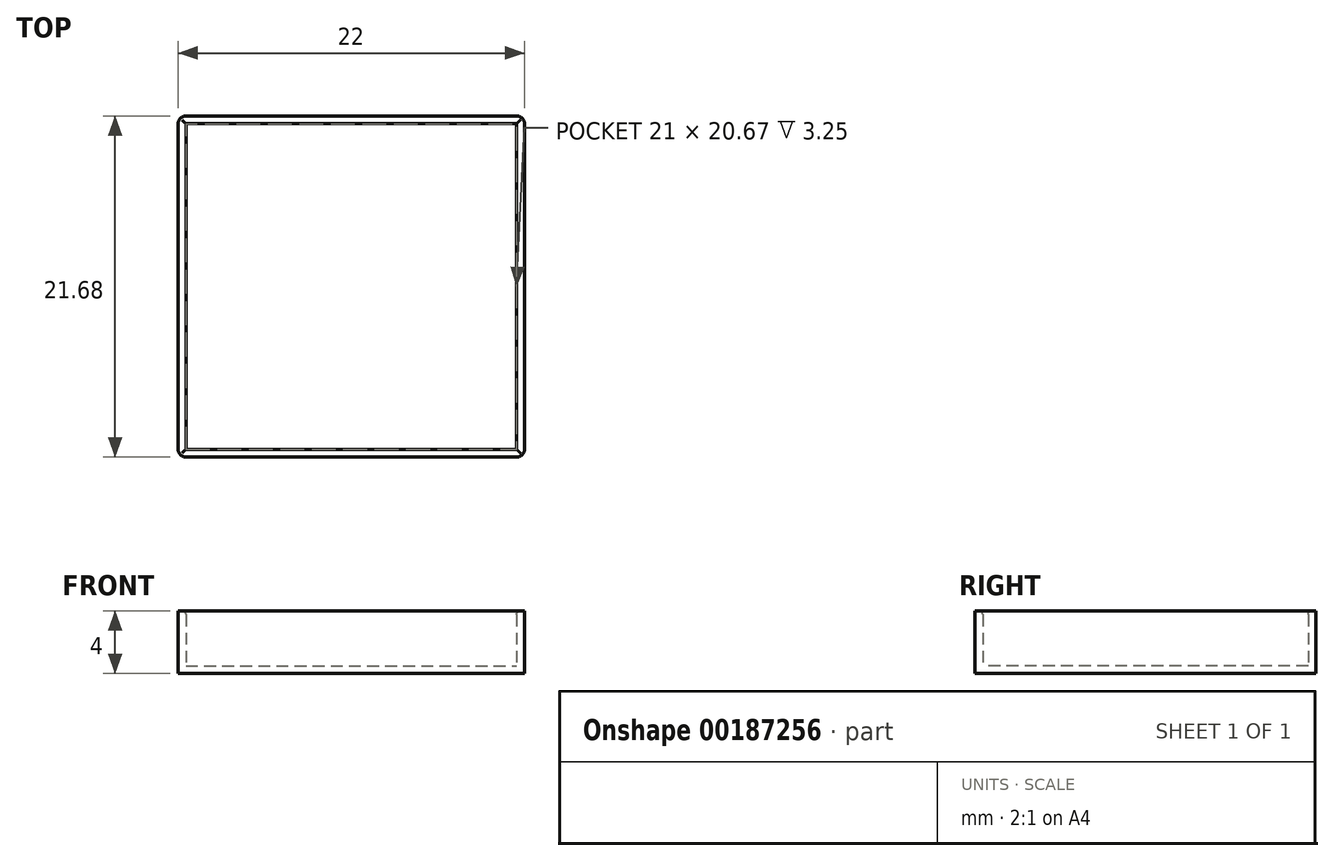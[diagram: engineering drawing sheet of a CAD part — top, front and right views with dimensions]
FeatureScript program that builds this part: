
annotation { "Feature Type Name" : "Feature", "Feature Type Description" : "" }
export const myFeature = defineFeature(function(context is Context, id is Id, definition is map)
    precondition{}
    {
        {
            var Q0;
            Q0=qCreatedBy(makeId("Top.planeOp"),FACE);
            var sketch = newSketch(context, id + "F0", { "sketchPlane" : qUnion([Q0])});
            skLineSegment(sketch, "E0.bottom", {"start": v(-10.5, 10.84) * mm, "end": v(10.5, 10.84) * mm});
            skLineSegment(sketch, "E0.top", {"start": v(-10.5, -10.84) * mm, "end": v(10.5, -10.84) * mm});
            skLineSegment(sketch, "E0.left", {"start": v(-11, 10.34) * mm, "end": v(-11, -10.34) * mm});
            skLineSegment(sketch, "E0.right", {"start": v(11, 10.34) * mm, "end": v(11, -10.34) * mm});
            skPoint(sketch, "E0.middle", {"position": v(0, 0) * mm});
            skPoint(sketch, "E1.visualSharp", {"position": v(-11, 10.84) * mm});
            skArc(sketch, "E1.filletArc", {"start": v(-10.5, 10.84) * mm, "mid": v(-10.85, 10.69) * mm, "end": v(-11, 10.34) * mm});
            skPoint(sketch, "E2.visualSharp", {"position": v(11, 10.84) * mm});
            skArc(sketch, "E2.filletArc", {"start": v(11, 10.34) * mm, "mid": v(10.85, 10.69) * mm, "end": v(10.5, 10.83) * mm});
            skPoint(sketch, "E3.visualSharp", {"position": v(11, -10.84) * mm});
            skArc(sketch, "E3.filletArc", {"start": v(10.5, -10.84) * mm, "mid": v(10.85, -10.69) * mm, "end": v(11, -10.34) * mm});
            skPoint(sketch, "E4.visualSharp", {"position": v(-11, -10.84) * mm});
            skArc(sketch, "E4.filletArc", {"start": v(-11, -10.34) * mm, "mid": v(-10.85, -10.69) * mm, "end": v(-10.5, -10.83) * mm});
            skSolve(sketch);
        }
        {
            var Q0;
            Q0=makeQuery(id+"F0.imprint","IMPRINT",FACE,{"disambiguationData":[TD([[makeQuery(id+"F0.imprint","IMPRINT",EDGE,{"derivedFrom":sQuery(id+"F0.wireOp",EDGE,"E0.bottom")}),-1.0]])]});
            extrude(context, id + "F1", {"entities" : qUnion([Q0]), "depth" : 4 * mm});
        }
        {
            var Q0;
            Q0=makeQuery(id+"F1.opExtrude","CAP_FACE",FACE,{"disambiguationData":[OSD([sQuery(id+"F0.wireOp",EDGE,"E0.bottom"),sQuery(id+"F0.wireOp",EDGE,"E0.top"),sQuery(id+"F0.wireOp",EDGE,"E0.left"),sQuery(id+"F0.wireOp",EDGE,"E0.right"),sQuery(id+"F0.wireOp",EDGE,"E1.filletArc"),sQuery(id+"F0.wireOp",EDGE,"E2.filletArc"),sQuery(id+"F0.wireOp",EDGE,"E3.filletArc"),sQuery(id+"F0.wireOp",EDGE,"E4.filletArc")])],"isStart":false});
            shell(context, id + "F2", {"entities" : qUnion([Q0]), "thickness" : .5 * mm});
        }
        {
            var Q0;
            {var subQ0=sQuery(id+"F0.wireOp",EDGE,"E0.right");Q0=makeQuery(id+"F2.opShell","OFFSET_EDGE",EDGE,{"disambiguationData":[OSD([subQ0]),TDD([makeQuery(id+"F1.opExtrude","CAP_EDGE",EDGE,{"disambiguationData":[OSD([subQ0])],"isStart":false})])]});}
            var Q1;
            {var subQ0=sQuery(id+"F0.wireOp",EDGE,"E0.bottom");Q1=makeQuery(id+"F2.opShell","OFFSET_EDGE",EDGE,{"disambiguationData":[OSD([subQ0]),TDD([makeQuery(id+"F1.opExtrude","CAP_EDGE",EDGE,{"disambiguationData":[OSD([subQ0])],"isStart":false})])]});}
            var Q2;
            {var subQ0=sQuery(id+"F0.wireOp",EDGE,"E0.left");Q2=makeQuery(id+"F2.opShell","OFFSET_EDGE",EDGE,{"disambiguationData":[OSD([subQ0]),TDD([makeQuery(id+"F1.opExtrude","CAP_EDGE",EDGE,{"disambiguationData":[OSD([subQ0])],"isStart":false})])]});}
            var Q3;
            {var subQ0=sQuery(id+"F0.wireOp",EDGE,"E0.top");Q3=makeQuery(id+"F2.opShell","OFFSET_EDGE",EDGE,{"disambiguationData":[OSD([subQ0]),TDD([makeQuery(id+"F1.opExtrude","CAP_EDGE",EDGE,{"disambiguationData":[OSD([subQ0])],"isStart":false})])]});}
            fillet(context, id + "F3", {"entities" : qUnion([Q0, Q1, Q2, Q3]), "radius" : .25 * mm, "tangentPropagation" : true, "allowEdgeOverflow" : false});
        }
    });
